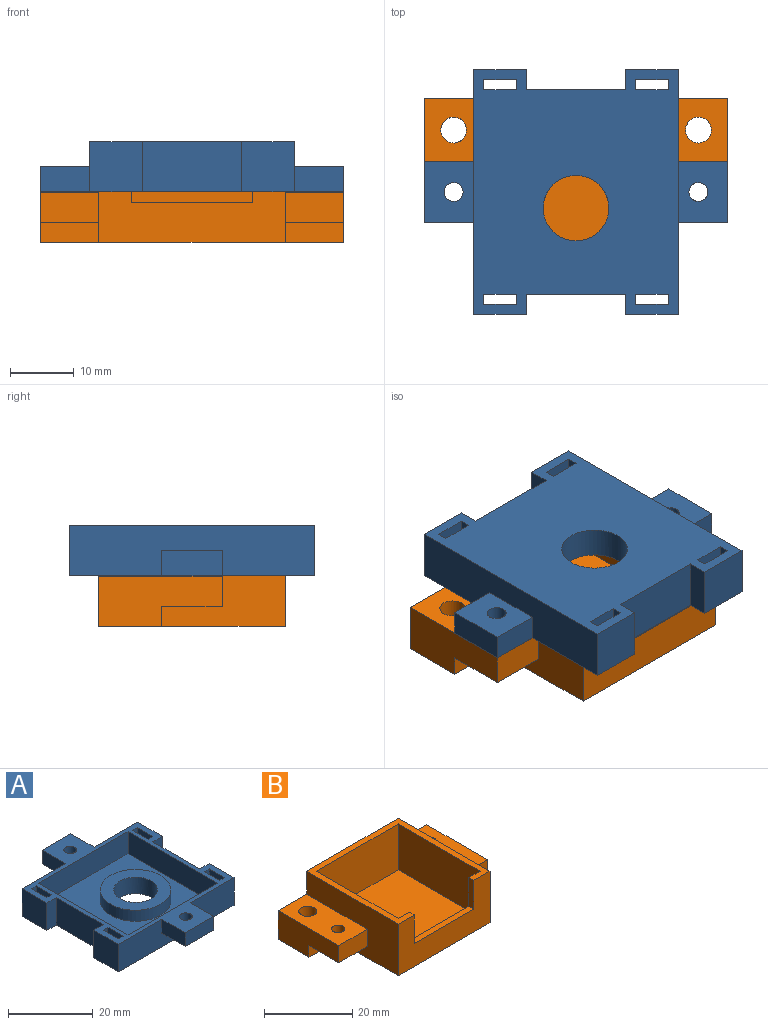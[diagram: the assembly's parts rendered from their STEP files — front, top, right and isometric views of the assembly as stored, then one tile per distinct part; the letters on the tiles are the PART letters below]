
ASSEMBLY  parts=2 mates=1
PART A: 48 faces, bbox 38.5x47.6x7.9 mm
  f0: plane 7.94x5.08mm, normal (1,0,0), area 40.3mm2, adj f6,f18,f43,f45
  f1: plane 7.94x5.08mm, normal (-1,0,0), area 40.3mm2, adj f6,f18,f40,f42
  f2: plane 15.64x7.94mm, normal (-1,0,0), area 124.1mm2, adj f6,f18,f37,f38
  f3: plane 7.94x5.08mm, normal (-1,0,0), area 40.3mm2, adj f6,f18,f33,f35
  f4: plane 15.64x7.94mm, normal (1,0,0), area 124.1mm2, adj f6,f18,f28,f46
  f5: plane 7.94x5.08mm, normal (1,0,0), area 40.3mm2, adj f6,f18,f30,f32
  f6: plane 38.5x32.15mm, normal (0,0,-1), area 1022.4mm2, adj f0,f1,f2,f3,f4,f5,f15,f16
  f7: cylinder r=1.5mm len=3.97mm, axis (0,0,-1), area 37.4mm2, adj f18,f26
  f8: plane 7.74x3.97mm, normal (1,0,0), area 30.7mm2, adj f10,f15,f18,f26
  f9: plane 7.74x3.97mm, normal (-1,0,0), area 30.7mm2, adj f10,f15,f18,f26
  f10: plane 9.53x3.97mm, normal (0,1,0), area 37.8mm2, adj f8,f9,f18,f26
  f11: plane 29.77x29.77mm, normal (0,0,1), area 667.8mm2, adj f12,f13,f14,f17,f20
  f12: plane 29.77x6.35mm, normal (0,-1,0), area 189mm2, adj f11,f13,f17,f18
  f13: plane 29.77x6.35mm, normal (-1,0,0), area 189mm2, adj f11,f12,f14,f18
  f14: plane 29.77x6.35mm, normal (0,1,0), area 189mm2, adj f11,f13,f17,f18
  f15: plane 38.5x7.94mm, normal (0,1,0), area 267.8mm2, adj f6,f8,f9,f18,f26,f39,f47
  f16: plane 38.5x7.94mm, normal (0,-1,0), area 267.8mm2, adj f6,f18,f22,f24,f27,f29,f36
  f17: plane 29.77x6.35mm, normal (1,0,0), area 189mm2, adj f11,f12,f14,f18
  f18: plane 47.63x38.5mm, normal (0,0,1), area 353.3mm2, adj f0,f1,f2,f3,f4,f5,f7,f8
  f19: cylinder r=5.16mm len=10.32mm, axis (0,0,-1), area 154.4mm2, adj f6,f21
  f20: cylinder r=8.33mm len=16.67mm, axis (0,0,-1), area 166.3mm2, adj f11,f21
  f21: plane 16.67x16.67mm, normal (0,0,1), area 134.6mm2, adj f19,f20
  f22: plane 7.74x3.97mm, normal (1,0,0), area 30.7mm2, adj f16,f18,f23,f27
  f23: plane 9.53x3.97mm, normal (0,-1,0), area 37.8mm2, adj f18,f22,f24,f27
  f24: plane 7.74x3.97mm, normal (-1,0,0), area 30.7mm2, adj f16,f18,f23,f27
  f25: cylinder r=1.5mm len=3.97mm, axis (0,0,-1), area 37.4mm2, adj f18,f27
  f26: plane 9.53x7.74mm, normal (0,0,-1), area 66.6mm2, adj f7,f8,f9,f10,f15
  f27: plane 9.53x7.74mm, normal (0,0,-1), area 66.6mm2, adj f16,f22,f23,f24,f25
  f28: plane 7.94x3.18mm, normal (0,1,0), area 25.2mm2, adj f4,f6,f18,f29
  f29: plane 8.26x7.94mm, normal (1,0,0), area 65.5mm2, adj f6,f16,f18,f28
  f30: plane 7.94x1.59mm, normal (0,1,0), area 12.6mm2, adj f5,f6,f18,f31
  f31: plane 7.94x5.08mm, normal (-1,0,0), area 40.3mm2, adj f6,f18,f30,f32
  f32: plane 7.94x1.59mm, normal (0,-1,0), area 12.6mm2, adj f5,f6,f18,f31
  f33: plane 7.94x1.59mm, normal (0,-1,0), area 12.6mm2, adj f3,f6,f18,f34
  f34: plane 7.94x5.08mm, normal (1,0,0), area 40.3mm2, adj f6,f18,f33,f35
  f35: plane 7.94x1.59mm, normal (0,1,0), area 12.6mm2, adj f3,f6,f18,f34
  f36: plane 8.26x7.94mm, normal (-1,0,0), area 65.5mm2, adj f6,f16,f18,f37
  f37: plane 7.94x3.18mm, normal (0,1,0), area 25.2mm2, adj f2,f6,f18,f36
  f38: plane 7.94x3.18mm, normal (0,-1,0), area 25.2mm2, adj f2,f6,f18,f39
  f39: plane 8.26x7.94mm, normal (-1,0,0), area 65.5mm2, adj f6,f15,f18,f38
  f40: plane 7.94x1.59mm, normal (0,-1,0), area 12.6mm2, adj f1,f6,f18,f41
  f41: plane 7.94x5.08mm, normal (1,0,0), area 40.3mm2, adj f6,f18,f40,f42
  f42: plane 7.94x1.59mm, normal (0,1,0), area 12.6mm2, adj f1,f6,f18,f41
  f43: plane 7.94x1.59mm, normal (0,1,0), area 12.6mm2, adj f0,f6,f18,f44
  f44: plane 7.94x5.08mm, normal (-1,0,0), area 40.3mm2, adj f6,f18,f43,f45
  f45: plane 7.94x1.59mm, normal (0,-1,0), area 12.6mm2, adj f0,f6,f18,f44
  f46: plane 7.94x3.18mm, normal (0,-1,0), area 25.2mm2, adj f4,f6,f18,f47
  f47: plane 8.26x7.94mm, normal (1,0,0), area 65.5mm2, adj f6,f15,f18,f46
PART B: 28 faces, bbox 47.6x29.4x14.3 mm
  f0: plane 29.37x14.29mm, normal (-1,0,0), area 295.5mm2, adj f5,f6,f8,f9,f19,f22,f23,f24
  f1: plane 26.19x12.7mm, normal (0,1,0), area 181.5mm2, adj f3,f7,f8,f10,f11,f12,f13
  f2: plane 26.19x12.7mm, normal (0,-1,0), area 332.7mm2, adj f3,f7,f8,f10
  f3: plane 26.19x12.7mm, normal (-1,0,0), area 332.7mm2, adj f1,f2,f8,f10
  f4: plane 29.37x14.29mm, normal (1,0,0), area 295.5mm2, adj f5,f6,f8,f9,f14,f17,f18,f26
  f5: plane 47.63x14.29mm, normal (0,1,0), area 564.5mm2, adj f0,f4,f8,f9,f16,f17,f20,f22
  f6: plane 29.37x14.29mm, normal (0,-1,0), area 268.4mm2, adj f0,f4,f8,f9,f11,f12,f13
  f7: plane 26.19x12.7mm, normal (1,0,0), area 332.7mm2, adj f1,f2,f8,f10
  f8: plane 29.37x29.37mm, normal (0,0,1), area 146.2mm2, adj f0,f1,f2,f3,f4,f5,f6,f7
  f9: plane 47.63x29.37mm, normal (0,0,-1), area 1017.7mm2, adj f0,f4,f5,f6,f16,f20,f24,f25
  f10: plane 26.19x26.19mm, normal (0,0,1), area 686.1mm2, adj f1,f2,f3,f7
  f11: plane 7.94x1.59mm, normal (1,0,0), area 12.6mm2, adj f1,f6,f8,f12
  f12: plane 19.05x1.59mm, normal (0,0,1), area 30.2mm2, adj f1,f6,f11,f13
  f13: plane 7.94x1.59mm, normal (-1,0,0), area 12.6mm2, adj f1,f6,f8,f12
  f14: plane 9.13x4.76mm, normal (0,-1,0), area 43.5mm2, adj f4,f16,f17,f18
  f15: cylinder r=1.5mm len=4.76mm, axis (0,0,-1), area 44.9mm2, adj f17,f18
  f16: plane 19.45x7.94mm, normal (1,0,0), area 124.1mm2, adj f5,f9,f14,f17,f18,f26
  f17: plane 19.45x9.13mm, normal (0,0,1), area 157.5mm2, adj f4,f5,f14,f15,f16,f27
  f18: plane 9.53x9.13mm, normal (0,0,-1), area 79.9mm2, adj f4,f14,f15,f16,f26
  f19: plane 9.13x4.76mm, normal (0,-1,0), area 43.5mm2, adj f0,f20,f22,f23
  f20: plane 19.45x7.94mm, normal (-1,0,0), area 124.1mm2, adj f5,f9,f19,f22,f23,f24
  f21: cylinder r=1.5mm len=4.76mm, axis (0,0,-1), area 44.9mm2, adj f22,f23
  f22: plane 19.45x9.13mm, normal (0,0,1), area 157.5mm2, adj f0,f5,f19,f20,f21,f25
  f23: plane 9.53x9.13mm, normal (0,0,-1), area 79.9mm2, adj f0,f19,f20,f21,f24
  f24: plane 9.13x3.18mm, normal (0,-1,0), area 29mm2, adj f0,f9,f20,f23
  f25: cylinder r=2.03mm len=7.94mm, axis (0,0,-1), area 101.3mm2, adj f9,f22
  f26: plane 9.13x3.18mm, normal (0,-1,0), area 29mm2, adj f4,f9,f16,f18
  f27: cylinder r=2.03mm len=7.94mm, axis (0,0,-1), area 101.3mm2, adj f9,f17
PLACE A rot(axis=(0.71,-0.71,0),180deg) t=(13.99,17.89,13.15)mm
PLACE B t=(13.99,17.91,-2.73)mm fixed
MATE planar A.f11 <-> B.f8  axis (0,0,-1) through (13.99,18.72,11.56)mm
